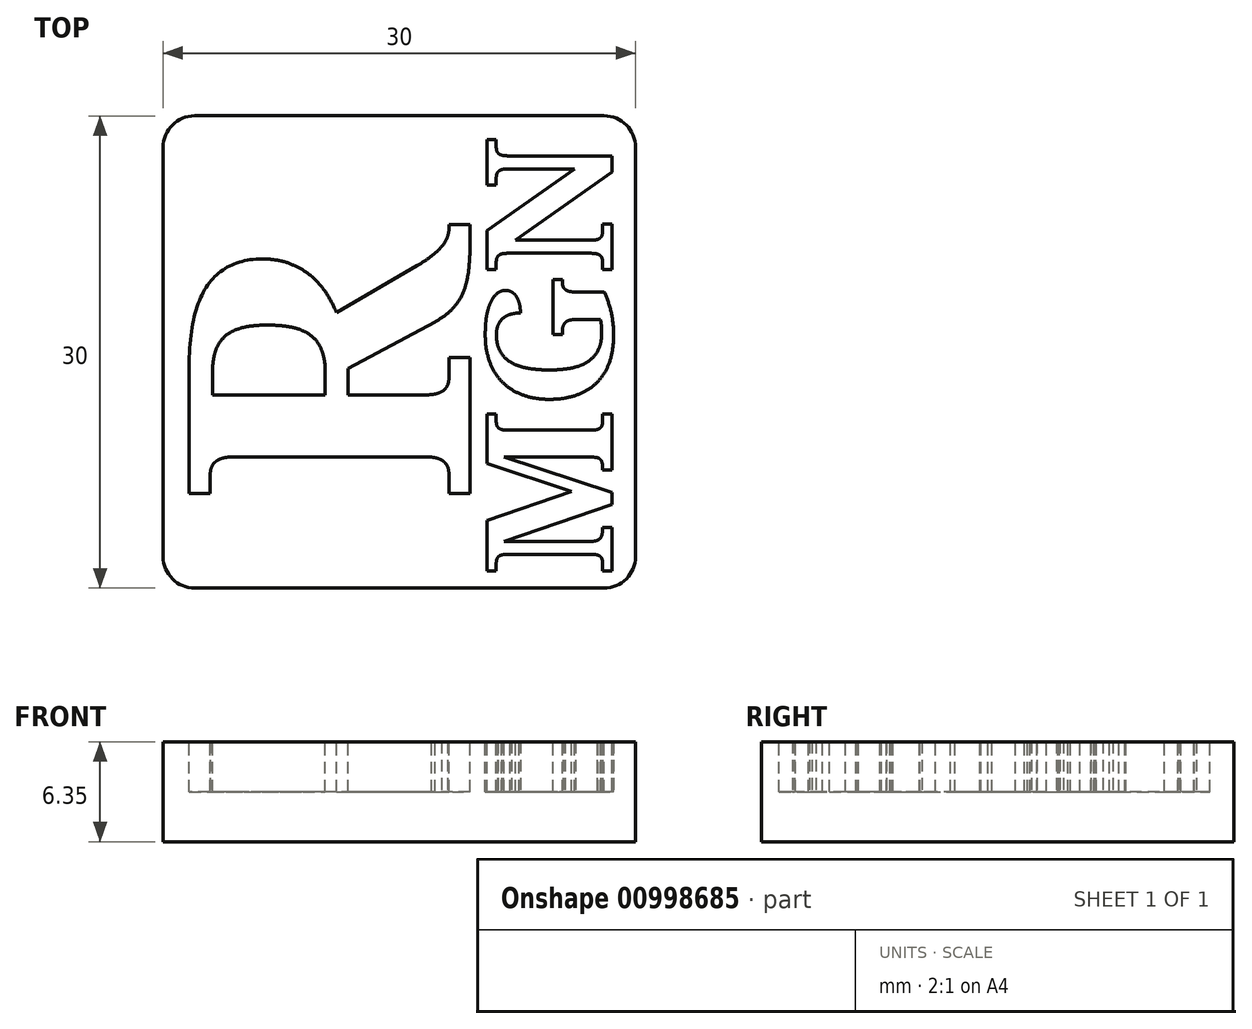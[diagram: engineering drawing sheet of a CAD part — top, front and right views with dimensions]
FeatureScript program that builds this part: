
annotation { "Feature Type Name" : "Feature", "Feature Type Description" : "" }
export const myFeature = defineFeature(function(context is Context, id is Id, definition is map)
    precondition{}
    {
        {
            var Q0;
            Q0=qCreatedBy(makeId("Top.planeOp"),FACE);
            var sketch = newSketch(context, id + "F0", { "sketchPlane" : qUnion([Q0])});
            skLineSegment(sketch, "E0.bottom", {"start": v(-15.27, 9.73) * mm, "end": v(10.73, 9.73) * mm});
            skLineSegment(sketch, "E0.top", {"start": v(-15.27, -20.27) * mm, "end": v(10.73, -20.27) * mm});
            skLineSegment(sketch, "E0.left", {"start": v(-17.27, 7.73) * mm, "end": v(-17.27, -18.27) * mm});
            skLineSegment(sketch, "E0.right", {"start": v(12.73, 7.73) * mm, "end": v(12.73, -18.27) * mm});
            skPoint(sketch, "E1.visualSharp", {"position": v(-17.27, 9.73) * mm});
            skArc(sketch, "E1.filletArc", {"start": v(-15.27, 9.73) * mm, "mid": v(-16.68, 9.15) * mm, "end": v(-17.27, 7.73) * mm});
            skPoint(sketch, "E2.visualSharp", {"position": v(12.73, 9.73) * mm});
            skArc(sketch, "E2.filletArc", {"start": v(12.73, 7.73) * mm, "mid": v(12.14, 9.15) * mm, "end": v(10.73, 9.73) * mm});
            skPoint(sketch, "E3.visualSharp", {"position": v(12.73, -20.27) * mm});
            skArc(sketch, "E3.filletArc", {"start": v(10.73, -20.27) * mm, "mid": v(12.14, -19.68) * mm, "end": v(12.73, -18.27) * mm});
            skPoint(sketch, "E4.visualSharp", {"position": v(-17.27, -20.27) * mm});
            skArc(sketch, "E4.filletArc", {"start": v(-17.27, -18.27) * mm, "mid": v(-16.68, -19.68) * mm, "end": v(-15.27, -20.27) * mm});
            skSolve(sketch);
        }
        {
            var Q0;
            Q0=qSketchRegion(id+"F0",true);
            extrude(context, id + "F1", {"entities" : qUnion([Q0]), "depth" : 6.35 * mm, "offsetDistance" : 25.4 * mm});
        }
        {
            var Q0;
            Q0=makeQuery(id+"F1.opExtrude","CAP_FACE",FACE,{"disambiguationData":[OSD([sQuery(id+"F0.wireOp",EDGE,"E0.bottom"),sQuery(id+"F0.wireOp",EDGE,"E0.top"),sQuery(id+"F0.wireOp",EDGE,"E0.left"),sQuery(id+"F0.wireOp",EDGE,"E0.right")])],"isStart":false});
            var sketch = newSketch(context, id + "F2", { "sketchPlane" : qUnion([Q0])});
            skText(sketch, "E5", { "text": "R", "fontName": "NotoSerif-Bold.ttf"});
            skText(sketch, "E6", { "text": "MGN", "fontName": "NotoSerif-Bold.ttf"});
            skPoint(sketch, "E7", {"position": v(-17.27, -5.27) * mm});
            skPoint(sketch, "E8", {"position": v(12.73, -5.27) * mm});
            const initialGuessF2  = {"E5": [0.00223, -0.01496, 0, 1, 0.018], "E6": [0.01123, -0.01947, 0, 1, 0.008]};
            skSetInitialGuess(sketch, initialGuessF2);
            skSolve(sketch);
        }
        {
            var Q0;
            Q0=qSketchRegion(id+"F2",true);
            extrude(context, id + "F3", {"entities" : qUnion([Q0]), "operationType" : NewBodyOperationType.REMOVE, "oppositeDirection" : true, "depth" : 3.17 * mm, "offsetDistance" : 25.4 * mm});
        }
    });
